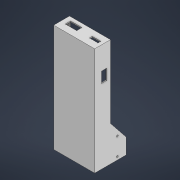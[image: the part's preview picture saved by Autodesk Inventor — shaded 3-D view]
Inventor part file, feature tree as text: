
AUTODESK INVENTOR PART (.ipt)
format: ipt  version: 2021 (Build 250183000, 183)  size: 378,368 bytes
history: native  units: in
note: dims shown in document units (in); Inventor stores cm internally (conversion verified against a paired STEP export)
features: extrude x8, sketch x8, shell x1
ambient origin geometry x8: Origin, YZ Plane, XZ Plane, XY Plane, X Axis, Y Axis, Z Axis, Center Point
bodies: Solid1 (feature_tree)
feature tree (17):
  extrude  "Extrusion1"  Depth=6.9in
  shell  "Shell1"  Thickness=2.0in
  sketch  "Sketch2"  dims[d4=0.0625in d5=0.375in]
  sketch  "Sketch4"  dims[d6=2.55in d7=0.1875in]
  extrude  "Extrusion2"  Depth=0.375in
  extrude  "Extrusion3"  Depth=0.1875in
  extrude  "Extrusion4"  Depth=0.72in
  extrude  "Extrusion5"  Depth=1.0in
  extrude  "Extrusion6"  Depth=0.375in
  extrude  "Extrusion7"  Depth=0.875in
  extrude  "Extrusion8"  Depth=1.0625in
  sketch  "Sketch1"  dims[d0=2.55in d1=6.9in d2=2.0in d3=0.0in]
  sketch  "Sketch5"  dims[d8=0.56in d9=0.72in]
  sketch  "Sketch6"  dims[d10=0.75in d11=1.0in]
  sketch  "Sketch7"  dims[d12=0.35in d13=0.375in]
  sketch  "Sketch8"  dims[d14=2.55in d15=0.875in]
  sketch  "Sketch9"  dims[d16=0.625in d17=1.0625in d18=0.5in d19=0.25in d20=1.3125in d21=0.375in d22=6.9in d23=0.7in d24=0.35in d25=2.12in d26=6.75in d27=0.0in d28=6.75in d29=0.0in d30=6.75in d31=0.0in d32=1.0in d33=6.75in d34=0.0in d35=0.1772in d36=0.205in d37=0.728in d38=0.1772in d39=1.378in d40=6.75in d41=0.0in d42=0.4331in d43=0.315in d44=0.689in d45=0.3937in d46=0.0in d47=0.1181in d48=0.1181in d49=1.1614in d50=0.1969in d51=0.5906in d52=0.5906in d53=0.3937in d54=0.0in]
